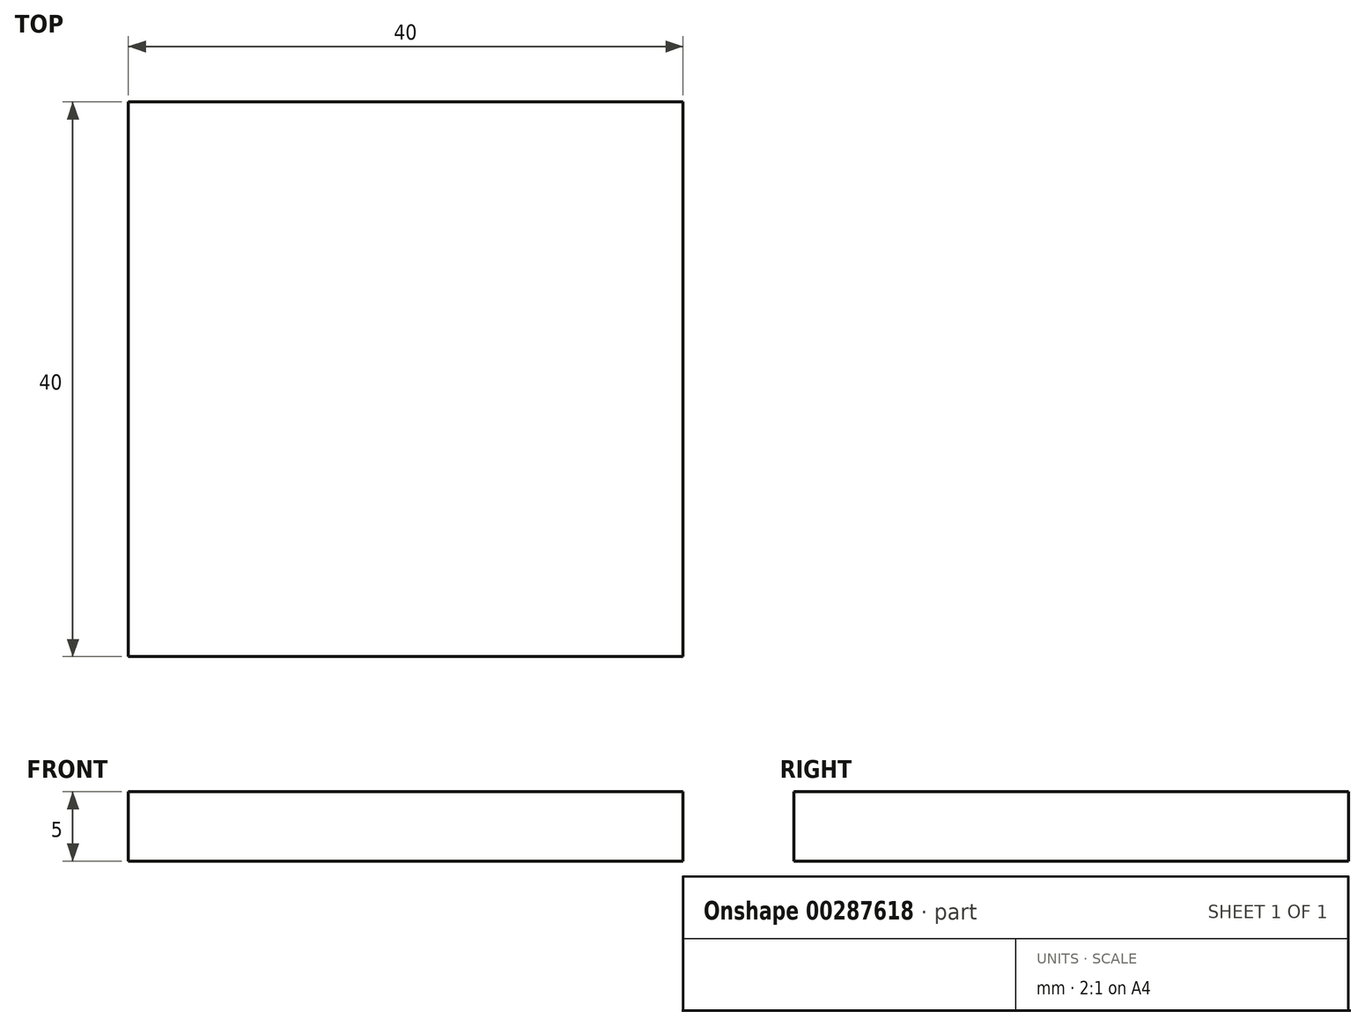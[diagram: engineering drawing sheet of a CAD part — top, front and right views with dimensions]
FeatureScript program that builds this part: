
annotation { "Feature Type Name" : "Feature", "Feature Type Description" : "" }
export const myFeature = defineFeature(function(context is Context, id is Id, definition is map)
    precondition{}
    {
        {
            var Q0;
            Q0=qCreatedBy(makeId("Top.planeOp"),FACE);
            var sketch = newSketch(context, id + "F0", { "sketchPlane" : qUnion([Q0])});
            skLineSegment(sketch, "E0.bottom", {"start": v(20, -20) * mm, "end": v(-20, -20) * mm});
            skLineSegment(sketch, "E0.top", {"start": v(20, 20) * mm, "end": v(-20, 20) * mm});
            skLineSegment(sketch, "E0.left", {"start": v(20, -20) * mm, "end": v(20, 20) * mm});
            skLineSegment(sketch, "E0.right", {"start": v(-20, -20) * mm, "end": v(-20, 20) * mm});
            skPoint(sketch, "E0.middle", {"position": v(0, 0) * mm});
            skSolve(sketch);
        }
        {
            var Q0;
            Q0 = qSketchRegion(id + "F0", true);
            extrude(context, id + "F1", {"entities" : qUnion([Q0]), "depth" : 5 * mm, "offsetDistance" : 25 * mm});
        }
    });
